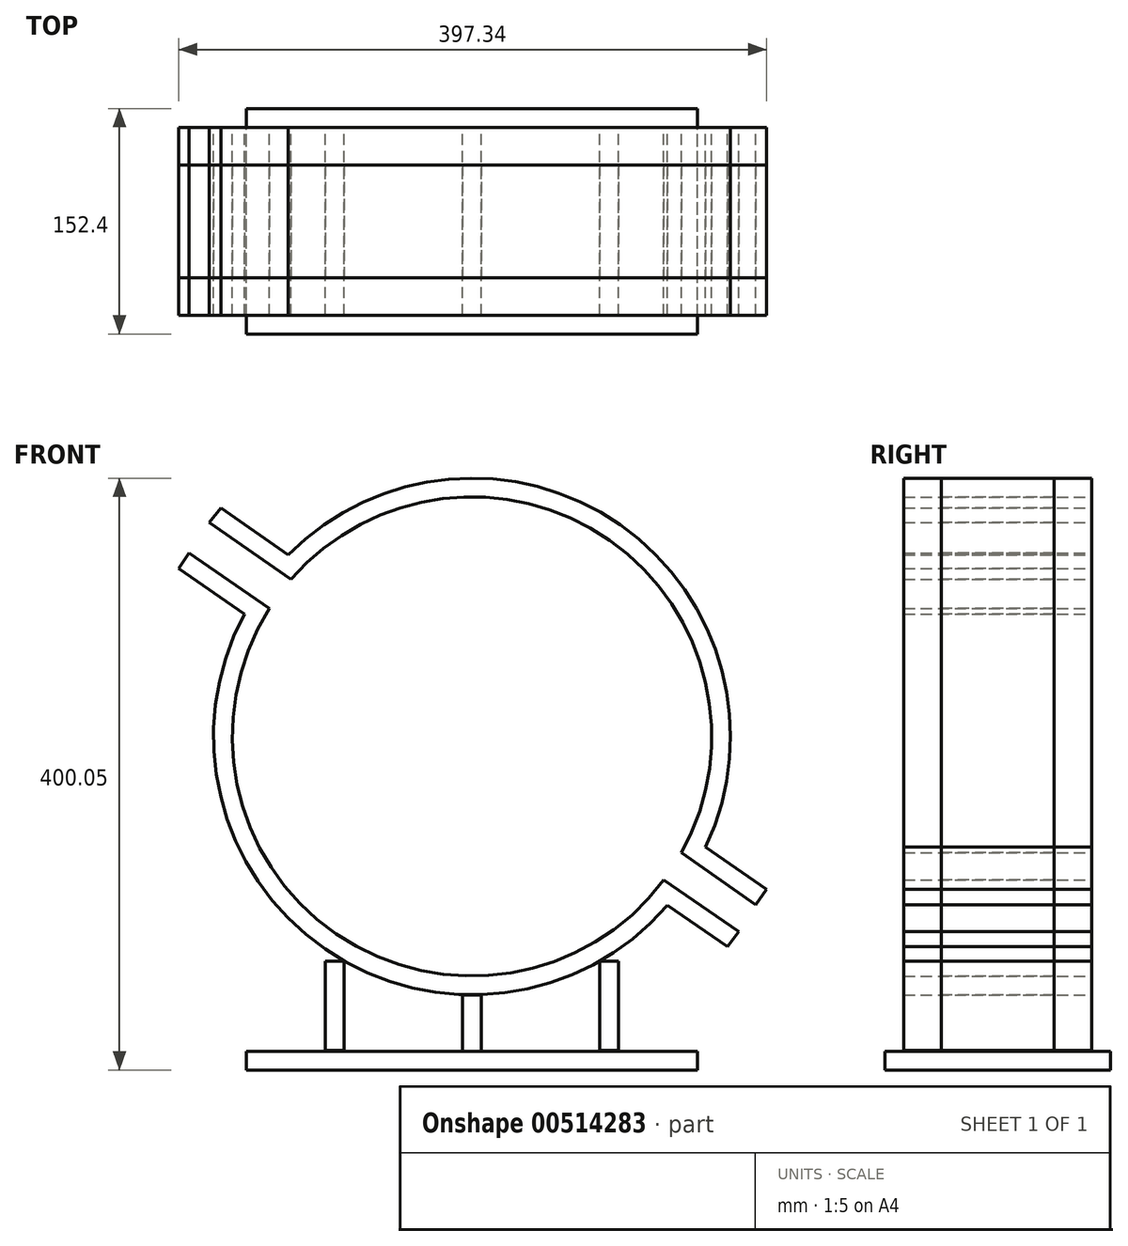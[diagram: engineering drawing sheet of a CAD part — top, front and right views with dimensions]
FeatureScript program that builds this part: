
annotation { "Feature Type Name" : "Feature", "Feature Type Description" : "" }
export const myFeature = defineFeature(function(context is Context, id is Id, definition is map)
    precondition{}
    {
        {
            var Q0;
            Q0=qCreatedBy(makeId("Top.planeOp"),FACE);
            var sketch = newSketch(context, id + "F0", { "sketchPlane" : qUnion([Q0])});
            skLineSegment(sketch, "E0.bottom", {"start": v(152.4, -76.2) * mm, "end": v(-152.4, -76.2) * mm});
            skLineSegment(sketch, "E0.top", {"start": v(152.4, 76.2) * mm, "end": v(-152.4, 76.2) * mm});
            skLineSegment(sketch, "E0.left", {"start": v(152.4, -76.2) * mm, "end": v(152.4, 76.2) * mm});
            skLineSegment(sketch, "E0.right", {"start": v(-152.4, -76.2) * mm, "end": v(-152.4, 76.2) * mm});
            skPoint(sketch, "E0.middle", {"position": v(0, 0) * mm});
            skSolve(sketch);
        }
        {
            var Q0;
            Q0 = qSketchRegion(id + "F0", true);
            extrude(context, id + "F1", {"entities" : qUnion([Q0]), "endBound" : BoundingType.SYMMETRIC, "depth" : 12.7 * mm});
        }
        {
            var Q0;
            Q0=qCreatedBy(makeId("Front.planeOp"),FACE);
            var sketch = newSketch(context, id + "F2", { "sketchPlane" : qUnion([Q0])});
            skLineSegment(sketch, "E1.bottom", {"start": v(6.35, 6.35) * mm, "end": v(-6.35, 6.35) * mm});
            skLineSegment(sketch, "E1.top", {"start": v(6.35, 44.45) * mm, "end": v(-6.35, 44.45) * mm});
            skLineSegment(sketch, "E1.left", {"start": v(6.35, 6.35) * mm, "end": v(6.35, 44.45) * mm});
            skLineSegment(sketch, "E1.right", {"start": v(-6.35, 6.35) * mm, "end": v(-6.35, 44.45) * mm});
            skPoint(sketch, "E1.middle", {"position": v(0, 25.4) * mm});
            skLineSegment(sketch, "E2.bottom", {"start": v(-86.3, 6.73) * mm, "end": v(-99, 6.73) * mm});
            skLineSegment(sketch, "E2.top", {"start": v(-86.3, 67.05) * mm, "end": v(-99, 67.05) * mm});
            skLineSegment(sketch, "E2.left", {"start": v(-86.3, 6.73) * mm, "end": v(-86.3, 67.05) * mm});
            skLineSegment(sketch, "E2.right", {"start": v(-99, 6.73) * mm, "end": v(-99, 67.05) * mm});
            skArc(sketch, "E3", {"start": v(-153.73, 301.9) * mm, "mid": v(-99.11, 75.3) * mm, "end": v(132.1, 104.87) * mm});
            skArc(sketch, "E4", {"start": v(-136.82, 305.68) * mm, "mid": v(-91.9, 85.76) * mm, "end": v(129.61, 122.02) * mm});
            skLineSegment(sketch, "E5.MirrorCS", {"start": v(86.3, 6.73) * mm, "end": v(86.3, 67.05) * mm});
            skLineSegment(sketch, "E6.MirrorCS", {"start": v(86.3, 67.05) * mm, "end": v(99, 67.05) * mm});
            skLineSegment(sketch, "E7.MirrorCS", {"start": v(99, 6.73) * mm, "end": v(99, 67.05) * mm});
            skLineSegment(sketch, "E8.MirrorCS", {"start": v(86.3, 6.73) * mm, "end": v(99, 6.73) * mm});
            skPoint(sketch, "E9.middle", {"position": v(0, 231.78) * mm});
            skLineSegment(sketch, "E10.MirrorCS", {"start": v(225.42, -225.43) * mm, "end": v(-225.43, -225.42) * mm});
            skLineSegment(sketch, "E11.MirrorCS", {"start": v(225.42, -238.13) * mm, "end": v(-225.43, -238.12) * mm});
            skPoint(sketch, "E12.middle", {"position": v(0, 206.38) * mm});
            skLineSegment(sketch, "E13", {"start": v(-177.52, 363.83) * mm, "end": v(-122.32, 325.18) * mm});
            skLineSegment(sketch, "E14", {"start": v(191.8, 105.23) * mm, "end": v(199.08, 115.63) * mm});
            skLineSegment(sketch, "E15", {"start": v(199.08, 115.63) * mm, "end": v(157.89, 144.48) * mm});
            skLineSegment(sketch, "E16", {"start": v(-169.5, 373.71) * mm, "end": v(-177.52, 363.83) * mm});
            skLineSegment(sketch, "E17", {"start": v(180.14, 87.18) * mm, "end": v(129.61, 122.02) * mm});
            skLineSegment(sketch, "E18", {"start": v(-191.06, 343.07) * mm, "end": v(-198.26, 332.61) * mm});
            skLineSegment(sketch, "E19", {"start": v(-198.26, 332.61) * mm, "end": v(-153.73, 301.9) * mm});
            skLineSegment(sketch, "E20", {"start": v(172.67, 76.9) * mm, "end": v(180.14, 87.18) * mm});
            skLineSegment(sketch, "E21.trimOffspring", {"start": v(-124.1, 341.93) * mm, "end": v(-169.5, 373.71) * mm});
            skLineSegment(sketch, "E22.trimOffspring", {"start": v(141.54, 140.42) * mm, "end": v(191.8, 105.23) * mm});
            skArc(sketch, "E23.trimOffspring", {"start": v(157.89, 144.48) * mm, "mid": v(100.16, 362.12) * mm, "end": v(-124.1, 341.93) * mm});
            skLineSegment(sketch, "E24.trimOffspring", {"start": v(132.1, 104.87) * mm, "end": v(172.67, 76.9) * mm});
            skArc(sketch, "E25.trimOffspring", {"start": v(141.54, 140.42) * mm, "mid": v(92.88, 351.72) * mm, "end": v(-122.32, 325.18) * mm});
            skLineSegment(sketch, "E26.trimOffspring", {"start": v(-136.82, 305.68) * mm, "end": v(-191.06, 343.07) * mm});
            skSolve(sketch);
        }
        {
            var Q0;
            Q0 = qSketchRegion(id + "F2", true);
            extrude(context, id + "F3", {"entities" : qUnion([Q0]), "operationType" : NewBodyOperationType.ADD, "endBound" : BoundingType.SYMMETRIC, "depth" : 127 * mm, "offsetDistance" : 25.4 * mm});
        }
        {
            var Q0;
            Q0 = qSketchRegion(id + "F2", true);
            extrude(context, id + "F4", {"entities" : qUnion([Q0]), "endBound" : BoundingType.SYMMETRIC, "oppositeDirection" : true, "depth" : 76.2 * mm, "offsetDistance" : 25.4 * mm});
        }
    });
